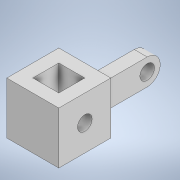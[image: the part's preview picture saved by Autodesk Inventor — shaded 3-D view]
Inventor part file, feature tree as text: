
AUTODESK INVENTOR PART (.ipt)
format: ipt  version: 2020.3 (Build 243373000, 373)  size: 141,312 bytes
history: native  units: mm
features: extrude x4, sketch x4, fillet x1
ambient origin geometry x8: Origin, YZ Plane, XZ Plane, XY Plane, X Axis, Y Axis, Z Axis, Center Point
bodies: Solid1 (feature_tree)
feature tree (9):
  extrude  "Extrusion1"  Depth=10.0mm
  extrude  "Extrusion2"  Depth=2.5mm
  extrude  "Extrusion3"  Depth=5.0mm
  extrude  "Extrusion4"  Depth=5.0mm
  fillet  "Fillet1"  Radius=5.0mm
  sketch  "Sketch1"  dims[d0=10.0mm d1=10.0mm]
  sketch  "Sketch2"  dims[d2=2.5mm d3=2.5mm]
  sketch  "Sketch3"  dims[d4=5.0mm d5=5.0mm]
  sketch  "Sketch4"  dims[d6=10.0mm d7=0.0mm d8=5.0mm d9=5.0mm d10=2.8mm d11=0.0mm d12=0.0mm d13=2.5mm d14=2.5mm d15=5.0mm d16=5.0mm d17=12.0mm d18=0.0mm d19=2.5mm d20=2.5mm d21=2.8mm d22=2.5mm d23=0.0mm d24=2.5mm]
